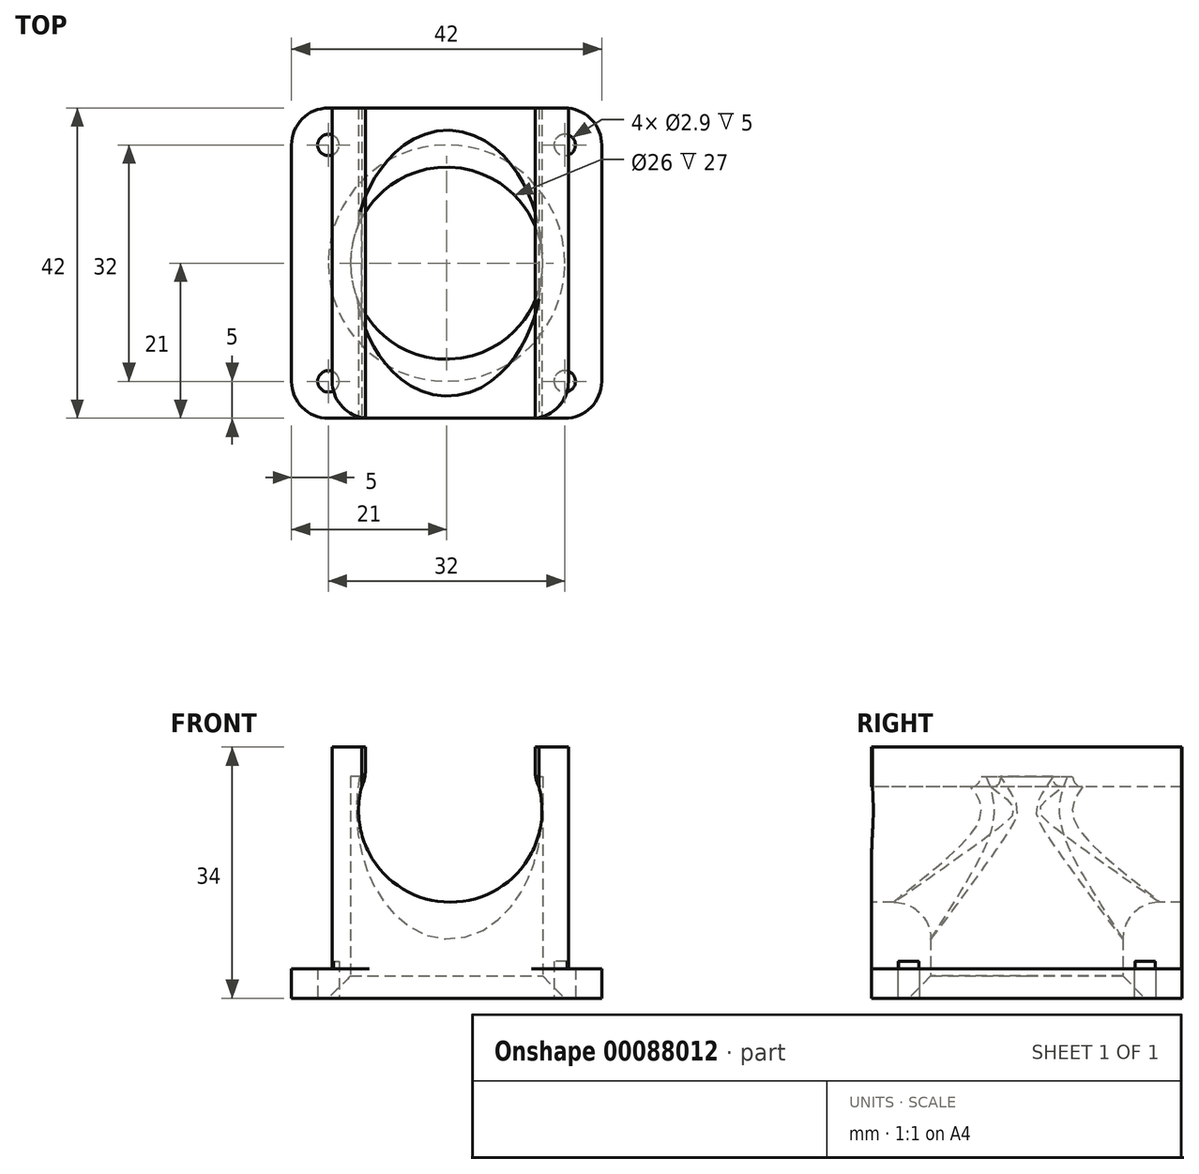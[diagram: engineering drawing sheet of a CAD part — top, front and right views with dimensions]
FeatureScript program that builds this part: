
annotation { "Feature Type Name" : "Feature", "Feature Type Description" : "" }
export const myFeature = defineFeature(function(context is Context, id is Id, definition is map)
    precondition{}
    {
        {
            var Q0;
            Q0=qCreatedBy(makeId("Top.planeOp"),FACE);
            var sketch = newSketch(context, id + "F0", { "sketchPlane" : qUnion([Q0])});
            skLineSegment(sketch, "E0.bottom", {"start": v(0, 0) * mm, "end": v(42, 0) * mm});
            skLineSegment(sketch, "E0.top", {"start": v(0, 42) * mm, "end": v(42, 42) * mm});
            skLineSegment(sketch, "E0.left", {"start": v(0, 0) * mm, "end": v(0, 42) * mm});
            skLineSegment(sketch, "E0.right", {"start": v(42, 0) * mm, "end": v(42, 42) * mm});
            skSolve(sketch);
        }
        {
            var Q0;
            Q0=qSketchRegion(id+"F0",true);
            extrude(context, id + "F1", {"entities" : qUnion([Q0]), "depth" : 4 * mm});
        }
        {
            var Q0;
            Q0=makeQuery(id+"F1.opExtrude","CAP_FACE",FACE,{"disambiguationData":[OSD([sQuery(id+"F0.wireOp",EDGE,"E0.bottom"),sQuery(id+"F0.wireOp",EDGE,"E0.top"),sQuery(id+"F0.wireOp",EDGE,"E0.left"),sQuery(id+"F0.wireOp",EDGE,"E0.right")])],"isStart":false});
            var sketch = newSketch(context, id + "F2", { "sketchPlane" : qUnion([Q0])});
            skLineSegment(sketch, "E1.bottom", {"start": v(5.5, 42) * mm, "end": v(37.5, 42) * mm});
            skLineSegment(sketch, "E1.top", {"start": v(5.5, 0) * mm, "end": v(37.5, 0) * mm});
            skLineSegment(sketch, "E1.left", {"start": v(5.5, 42) * mm, "end": v(5.5, 0) * mm});
            skLineSegment(sketch, "E1.right", {"start": v(37.5, 42) * mm, "end": v(37.5, 0) * mm});
            skLineSegment(sketch, "E2", {"start": v(37.5, 21) * mm, "end": v(42, 21) * mm});
            skSolve(sketch);
        }
        {
            var Q0;
            Q0=qSketchRegion(id+"F2",true);
            extrude(context, id + "F3", {"entities" : qUnion([Q0]), "operationType" : NewBodyOperationType.ADD, "depth" : 30 * mm});
        }
        {
            var Q0;
            Q0=makeQuery(id+"F1.opExtrude","CAP_FACE",FACE,{"disambiguationData":[OSD([sQuery(id+"F0.wireOp",EDGE,"E0.bottom"),sQuery(id+"F0.wireOp",EDGE,"E0.top"),sQuery(id+"F0.wireOp",EDGE,"E0.left"),sQuery(id+"F0.wireOp",EDGE,"E0.right")])],"isStart":true});
            var sketch = newSketch(context, id + "F4", { "sketchPlane" : qUnion([Q0])});
            skCircle(sketch, "E3", {"center": v(21, -21) * mm, "radius": 19 * mm});
            skLineSegment(sketch, "E4", {"start": v(21, -21) * mm, "end": v(21, 0) * mm});
            skLineSegment(sketch, "E5", {"start": v(21, -21) * mm, "end": v(42, -21) * mm});
            skSolve(sketch);
        }
        {
            var Q0;
            Q0=qSketchRegion(id+"F4",true);
            extrude(context, id + "F5", {"entities" : qUnion([Q0]), "operationType" : NewBodyOperationType.REMOVE, "oppositeDirection" : true, "depth" : 3 * mm});
        }
        {
            var Q0;
            Q0=makeQuery(id+"F5.boolean.opBoolean","COPY",FACE,{"derivedFrom":makeQuery(id+"F5.opExtrude","CAP_FACE",FACE,{"disambiguationData":[OSD([sQuery(id+"F4.wireOp",EDGE,"E3")])],"isStart":false})});
            var sketch = newSketch(context, id + "F6", { "sketchPlane" : qUnion([Q0])});
            skCircle(sketch, "E6", {"center": v(21, -21) * mm, "radius": 13 * mm});
            skSolve(sketch);
        }
        {
            var Q0;
            Q0=qSketchRegion(id+"F6",true);
            extrude(context, id + "F7", {"entities" : qUnion([Q0]), "operationType" : NewBodyOperationType.REMOVE, "oppositeDirection" : true, "depth" : 27 * mm});
        }
        {
            var Q0;
            Q0=makeQuery(id+"F3.opExtrude","SWEPT_FACE",FACE,{"disambiguationData":[OSD([sQuery(id+"F2.wireOp",EDGE,"E1.top")])]});
            var sketch = newSketch(context, id + "F8", { "sketchPlane" : qUnion([Q0])});
            skLineSegment(sketch, "E7", {"start": v(9.5, 34) * mm, "end": v(9.5, 28.62) * mm});
            skLineSegment(sketch, "E8", {"start": v(33.5, 34) * mm, "end": v(33.5, 28.62) * mm});
            skLineSegment(sketch, "E9", {"start": v(9.5, 28.62) * mm, "end": v(5.5, 28.62) * mm, "construction": true});
            skLineSegment(sketch, "E10", {"start": v(33.5, 28.62) * mm, "end": v(37.5, 28.62) * mm, "construction": true});
            skCircle(sketch, "E11", {"center": v(21.5, 25.42) * mm, "radius": 12.42 * mm});
            skSolve(sketch);
        }
        {
            var Q0;
            Q0=qSketchRegion(id+"F8",true);
            var Q1;
            {var subQ3=sQuery(id+"F8.wireOp",EDGE,"E7");Q1=makeQuery(id+"F8.imprint","IMPRINT",FACE,{"disambiguationData":[TD([[makeQuery(id+"F8.imprint","IMPRINT",EDGE,{"derivedFrom":subQ3}),1.0]])]});}
            var Q2;
            {var subQ3=sQuery(id+"F8.wireOp",EDGE,"E8");Q2=makeQuery(id+"F8.imprint","IMPRINT",FACE,{"disambiguationData":[TD([[makeQuery(id+"F8.imprint","IMPRINT",EDGE,{"derivedFrom":subQ3}),-1.0]])]});}
            extrude(context, id + "F9", {"entities" : qUnion([Q0, Q1, Q2]), "operationType" : NewBodyOperationType.REMOVE, "endBound" : BoundingType.THROUGH_ALL, "oppositeDirection" : true, "depth" : 25 * mm});
        }
        {
            var Q0;
            Q0=makeQuery(id+"F1.opExtrude","SWEPT_EDGE",EDGE,{"disambiguationData":[OSD([sQuery(id+"F0.wireOp",EDGE,"E0.top"),sQuery(id+"F0.wireOp",EDGE,"E0.right")])]});
            var Q1;
            Q1=makeQuery(id+"F1.opExtrude","SWEPT_EDGE",EDGE,{"disambiguationData":[OSD([sQuery(id+"F0.wireOp",EDGE,"E0.top"),sQuery(id+"F0.wireOp",EDGE,"E0.left")])]});
            var Q2;
            Q2=makeQuery(id+"F1.opExtrude","SWEPT_EDGE",EDGE,{"disambiguationData":[OSD([sQuery(id+"F0.wireOp",EDGE,"E0.bottom"),sQuery(id+"F0.wireOp",EDGE,"E0.left")])]});
            var Q3;
            Q3=makeQuery(id+"F1.opExtrude","SWEPT_EDGE",EDGE,{"disambiguationData":[OSD([sQuery(id+"F0.wireOp",EDGE,"E0.bottom"),sQuery(id+"F0.wireOp",EDGE,"E0.right")])]});
            fillet(context, id + "F10", {"entities" : qUnion([Q0, Q1, Q2, Q3]), "radius" : 5 * mm, "tangentPropagation" : true, "allowEdgeOverflow" : false});
        }
        {
            var Q0;
            Q0=makeQuery(id+"F3.opExtrude","SWEPT_EDGE",EDGE,{"disambiguationData":[OSD([sQuery(id+"F2.wireOp",EDGE,"E1.top"),sQuery(id+"F2.wireOp",EDGE,"E1.left")])]});
            var Q1;
            Q1=makeQuery(id+"F3.opExtrude","SWEPT_EDGE",EDGE,{"disambiguationData":[OSD([sQuery(id+"F2.wireOp",EDGE,"E1.top"),sQuery(id+"F2.wireOp",EDGE,"E1.right")])]});
            var Q2;
            Q2=makeQuery(id+"F10.opFillet","BLEND_EDGE",EDGE,{"blendedFrom":[makeQuery(id+"F1.opExtrude","SWEPT_EDGE",EDGE,{"disambiguationData":[OSD([sQuery(id+"F0.wireOp",EDGE,"E0.bottom"),sQuery(id+"F0.wireOp",EDGE,"E0.right")])]}),makeQuery(id+"F3.opExtrude","SWEPT_FACE",FACE,{"disambiguationData":[OSD([sQuery(id+"F2.wireOp",EDGE,"E1.right")])]})],"blendedInto":[makeQuery(id+"F3.opExtrude","SWEPT_FACE",FACE,{"disambiguationData":[OSD([sQuery(id+"F2.wireOp",EDGE,"E1.right")])]})]});
            fillet(context, id + "F11", {"entities" : qUnion([Q0, Q1, Q2]), "radius" : 5 * mm, "tangentPropagation" : true, "allowEdgeOverflow" : false});
        }
        {
            var Q0;
            {var subQ0=sQuery(id+"F8.wireOp",EDGE,"E11");Q0=makeQuery(id+"F9.boolean.opBoolean","INTERSECT",EDGE,{"derivedFrom":[makeQuery(id+"F7.boolean.opBoolean","COPY",FACE,{"derivedFrom":makeQuery(id+"F7.opExtrude","SWEPT_FACE",FACE,{"disambiguationData":[OSD([sQuery(id+"F6.wireOp",EDGE,"E6")])]})}),makeQuery(id+"F9.opExtrude","SWEPT_FACE",FACE,{"disambiguationData":[OSD([subQ0]),TDD([makeQuery(id+"F8.imprint","IMPRINT",EDGE,{"disambiguationData":[TD([[makeQuery(id+"F8.imprint","INTERSECT",VERTEX,{"derivedFrom":[sQuery(id+"F8.wireOp",EDGE,"E7"),subQ0]}),-1.0]])],"derivedFrom":subQ0})])]})]});}
            fillet(context, id + "F12", {"entities" : qUnion([Q0]), "radius" : 5 * mm, "tangentPropagation" : true, "allowEdgeOverflow" : false});
        }
        {
            var Q0;
            Q0=makeQuery(id+"F1.opExtrude","CAP_FACE",FACE,{"disambiguationData":[OSD([sQuery(id+"F0.wireOp",EDGE,"E0.bottom"),sQuery(id+"F0.wireOp",EDGE,"E0.top"),sQuery(id+"F0.wireOp",EDGE,"E0.left"),sQuery(id+"F0.wireOp",EDGE,"E0.right")])],"isStart":true});
            var sketch = newSketch(context, id + "F13", { "sketchPlane" : qUnion([Q0])});
            skCircle(sketch, "E12", {"center": v(5, -5) * mm, "radius": 1.45 * mm});
            skCircle(sketch, "E13", {"center": v(37, -5) * mm, "radius": 1.45 * mm});
            skCircle(sketch, "E14", {"center": v(37, -37) * mm, "radius": 1.45 * mm});
            skCircle(sketch, "E15", {"center": v(5, -37) * mm, "radius": 1.45 * mm});
            skSolve(sketch);
        }
        {
            var Q0;
            Q0=qSketchRegion(id+"F13",true);
            extrude(context, id + "F14", {"entities" : qUnion([Q0]), "operationType" : NewBodyOperationType.REMOVE, "oppositeDirection" : true, "depth" : 5 * mm});
        }
        {
            var Q0;
            Q0=makeQuery(id+"F5.boolean.opBoolean","COPY",EDGE,{"derivedFrom":makeQuery(id+"F5.opExtrude","CAP_EDGE",EDGE,{"disambiguationData":[OSD([sQuery(id+"F4.wireOp",EDGE,"E3")])],"isStart":false})});
            chamfer(context, id + "F15", {"entities" : qUnion([Q0]), "width" : 6 * mm, "tangentPropagation" : true});
        }
        {
            var Q0;
            Q0=makeQuery(id+"F9.boolean.opBoolean","COPY",FACE,{"derivedFrom":makeQuery(id+"F9.opExtrude","SWEPT_FACE",FACE,{"disambiguationData":[OSD([sQuery(id+"F8.wireOp",EDGE,"E7")])]})});
            var sketch = newSketch(context, id + "F16", { "sketchPlane" : qUnion([Q0])});
            skLineSegment(sketch, "E16.bottom", {"start": v(0.1, 34) * mm, "end": v(42, 34) * mm});
            skLineSegment(sketch, "E16.top", {"start": v(0.1, 28.62) * mm, "end": v(42, 28.62) * mm});
            skLineSegment(sketch, "E16.left", {"start": v(0.1, 34) * mm, "end": v(0.1, 28.62) * mm});
            skLineSegment(sketch, "E16.right", {"start": v(42, 34) * mm, "end": v(42, 28.62) * mm});
            skSolve(sketch);
        }
        {
            var Q0;
            Q0=qSketchRegion(id+"F16",true);
            extrude(context, id + "F17", {"entities" : qUnion([Q0]), "operationType" : NewBodyOperationType.ADD, "depth" : 0.5 * mm});
        }
        {
            var Q0;
            Q0=makeQuery(id+"F9.boolean.opBoolean","COPY",FACE,{"derivedFrom":makeQuery(id+"F9.opExtrude","SWEPT_FACE",FACE,{"disambiguationData":[OSD([sQuery(id+"F8.wireOp",EDGE,"E8")])]})});
            var sketch = newSketch(context, id + "F18", { "sketchPlane" : qUnion([Q0])});
            skLineSegment(sketch, "E17.bottom", {"start": v(-42, 34) * mm, "end": v(0, 34) * mm});
            skLineSegment(sketch, "E17.top", {"start": v(-42, 28.62) * mm, "end": v(0, 28.62) * mm});
            skLineSegment(sketch, "E17.left", {"start": v(-42, 34) * mm, "end": v(-42, 28.62) * mm});
            skLineSegment(sketch, "E17.right", {"start": v(0, 34) * mm, "end": v(0, 28.62) * mm});
            skSolve(sketch);
        }
        {
            var Q0;
            Q0=qSketchRegion(id+"F18",true);
            extrude(context, id + "F19", {"entities" : qUnion([Q0]), "operationType" : NewBodyOperationType.ADD, "depth" : 0.5 * mm});
        }
        {
            var Q0;
            Q0=makeQuery(id+"F19.opExtrude","CAP_EDGE",EDGE,{"disambiguationData":[OSD([sQuery(id+"F18.wireOp",EDGE,"E17.top")])],"isStart":false});
            var Q1;
            Q1=makeQuery(id+"F17.opExtrude","CAP_EDGE",EDGE,{"disambiguationData":[OSD([sQuery(id+"F16.wireOp",EDGE,"E16.top")])],"isStart":false});
            fillet(context, id + "F20", {"entities" : qUnion([Q0, Q1]), "radius" : 5 * mm, "tangentPropagation" : true, "allowEdgeOverflow" : false});
        }
    });
